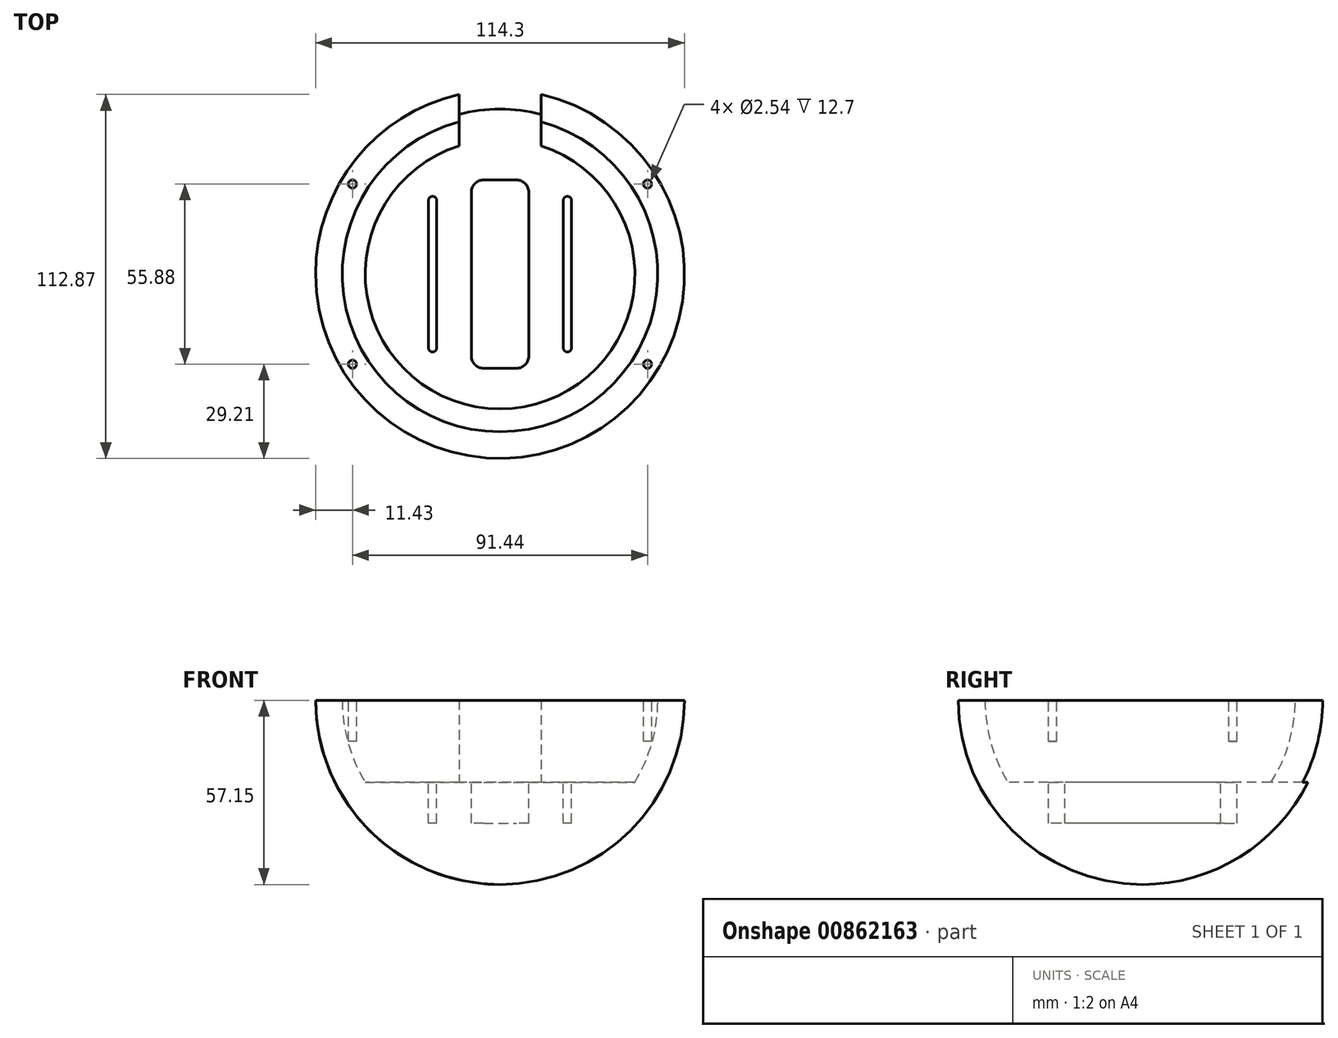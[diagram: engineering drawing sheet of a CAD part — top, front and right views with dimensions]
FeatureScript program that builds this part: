
annotation { "Feature Type Name" : "Feature", "Feature Type Description" : "" }
export const myFeature = defineFeature(function(context is Context, id is Id, definition is map)
    precondition{}
    {
        {
            var Q0;
            Q0=qCreatedBy(makeId("Front.planeOp"),FACE);
            var sketch = newSketch(context, id + "F0", { "sketchPlane" : qUnion([Q0])});
            skArc(sketch, "E0", {"start": v(-57.15, 0) * mm, "mid": v(-40.41, -40.41) * mm, "end": v(0, -57.15) * mm});
            skLineSegment(sketch, "E1", {"start": v(0, -25.4) * mm, "end": v(0, -57.15) * mm});
            skLineSegment(sketch, "E2", {"start": v(0, -57.15) * mm, "end": v(0, -25.4) * mm, "construction": true});
            skPoint(sketch, "E3.start.orphan", {"position": v(0, 31.75) * mm});
            skArc(sketch, "E4", {"start": v(-48.9, 0) * mm, "mid": v(-47.08, -13.19) * mm, "end": v(-41.78, -25.4) * mm});
            skLineSegment(sketch, "E5", {"start": v(0, -25.4) * mm, "end": v(-41.78, -25.4) * mm});
            skLineSegment(sketch, "E6", {"start": v(-57.15, 0) * mm, "end": v(-48.9, 0) * mm});
            skSolve(sketch);
        }
        {
            var Q0;
            Q0=makeQuery(id+"F0.imprint","IMPRINT",FACE,{"disambiguationData":[TD([[makeQuery(id+"F0.imprint","IMPRINT",EDGE,{"derivedFrom":sQuery(id+"F0.wireOp",EDGE,"E0")}),1.0]])]});
            var Q1;
            Q1=sQuery(id+"F0.wireOp",EDGE,"E1");
            revolve(context, id + "F1", {"surfaceOperationType" : NewSurfaceOperationType.NEW, "entities" : qUnion([Q0]), "axis" : qUnion([Q1]), "revolveType" : RevolveType.FULL});
        }
        {
            var Q0;
            Q0=makeQuery(id+"F1.opRevolve","SWEPT_FACE",FACE,{"disambiguationData":[OSD([sQuery(id+"F0.wireOp",EDGE,"E6")])]});
            var sketch = newSketch(context, id + "F2", { "sketchPlane" : qUnion([Q0])});
            skLineSegment(sketch, "E7", {"start": v(0, 0) * mm, "end": v(45.72, 0) * mm, "construction": true});
            skLineSegment(sketch, "E8", {"start": v(45.72, 0) * mm, "end": v(45.72, 27.94) * mm, "construction": true});
            skCircle(sketch, "E9", {"center": v(45.72, 27.94) * mm, "radius": 1.27 * mm});
            skCircle(sketch, "E10.MirrorC", {"center": v(45.72, -27.94) * mm, "radius": 1.27 * mm});
            skLineSegment(sketch, "E11.MirrorCS", {"start": v(45.72, 0) * mm, "end": v(45.72, -27.94) * mm, "construction": true});
            skLineSegment(sketch, "E12", {"start": v(0, 0) * mm, "end": v(0, -28.9) * mm, "construction": true});
            skCircle(sketch, "E13.MirrorC", {"center": v(-45.72, -27.94) * mm, "radius": 1.27 * mm});
            skCircle(sketch, "E14.MirrorC", {"center": v(-45.72, 27.94) * mm, "radius": 1.27 * mm});
            skSolve(sketch);
        }
        {
            var Q0;
            Q0 = qSketchRegion(id + "F2", true);
            extrude(context, id + "F3", {"entities" : qUnion([Q0]), "operationType" : NewBodyOperationType.REMOVE, "oppositeDirection" : true, "depth" : 12.7 * mm, "offsetDistance" : 25.4 * mm});
        }
        {
            var Q0;
            Q0=makeQuery(id+"F1.opRevolve","SWEPT_FACE",FACE,{"disambiguationData":[OSD([sQuery(id+"F0.wireOp",EDGE,"E5")])]});
            var sketch = newSketch(context, id + "F4", { "sketchPlane" : qUnion([Q0])});
            skLineSegment(sketch, "E15", {"start": v(0, 0) * mm, "end": v(41.78, 0) * mm, "construction": true});
            skLineSegment(sketch, "E16", {"start": v(0, 0) * mm, "end": v(-41.78, 0) * mm, "construction": true});
            skLineSegment(sketch, "E17", {"start": v(-20.89, 0) * mm, "end": v(-20.89, 22.86) * mm});
            skLineSegment(sketch, "E18", {"start": v(20.89, 0) * mm, "end": v(20.89, 22.86) * mm});
            skLineSegment(sketch, "E19.MirrorCS", {"start": v(-20.89, 0) * mm, "end": v(-20.89, -22.86) * mm});
            skLineSegment(sketch, "E20.MirrorCS", {"start": v(20.89, 0) * mm, "end": v(20.89, -22.86) * mm});
            skArc(sketch, "E21.0.startCap", {"start": v(-19.62, 0) * mm, "mid": v(-20.89, -1.27) * mm, "end": v(-22.16, 0) * mm});
            skArc(sketch, "E21.0.endCap", {"start": v(-22.16, 22.86) * mm, "mid": v(-20.89, 24.13) * mm, "end": v(-19.62, 22.86) * mm});
            skLineSegment(sketch, "E21.0.left", {"start": v(-22.16, 0) * mm, "end": v(-22.16, 22.86) * mm});
            skLineSegment(sketch, "E21.0.right", {"start": v(-19.62, 0) * mm, "end": v(-19.62, 22.86) * mm});
            skArc(sketch, "E21.1.startCap", {"start": v(-22.16, 0) * mm, "mid": v(-20.89, 1.27) * mm, "end": v(-19.62, 0) * mm});
            skArc(sketch, "E21.1.endCap", {"start": v(-19.62, -22.86) * mm, "mid": v(-20.89, -24.13) * mm, "end": v(-22.16, -22.86) * mm});
            skLineSegment(sketch, "E21.1.left", {"start": v(-19.62, 0) * mm, "end": v(-19.62, -22.86) * mm});
            skLineSegment(sketch, "E21.1.right", {"start": v(-22.16, 0) * mm, "end": v(-22.16, -22.86) * mm});
            skArc(sketch, "E22.0.startCap", {"start": v(22.16, 0) * mm, "mid": v(20.89, -1.27) * mm, "end": v(19.62, 0) * mm});
            skArc(sketch, "E22.0.endCap", {"start": v(19.62, 22.86) * mm, "mid": v(20.89, 24.13) * mm, "end": v(22.16, 22.86) * mm});
            skLineSegment(sketch, "E22.0.left", {"start": v(19.62, 0) * mm, "end": v(19.62, 22.86) * mm});
            skLineSegment(sketch, "E22.0.right", {"start": v(22.16, 0) * mm, "end": v(22.16, 22.86) * mm});
            skArc(sketch, "E22.1.startCap", {"start": v(19.62, 0) * mm, "mid": v(20.89, 1.27) * mm, "end": v(22.16, 0) * mm});
            skArc(sketch, "E22.1.endCap", {"start": v(22.16, -22.86) * mm, "mid": v(20.89, -24.13) * mm, "end": v(19.62, -22.86) * mm});
            skLineSegment(sketch, "E22.1.left", {"start": v(22.16, 0) * mm, "end": v(22.16, -22.86) * mm});
            skLineSegment(sketch, "E22.1.right", {"start": v(19.62, 0) * mm, "end": v(19.62, -22.86) * mm});
            skLineSegment(sketch, "E23.bottom", {"start": v(-5.08, 29.21) * mm, "end": v(5.08, 29.21) * mm});
            skLineSegment(sketch, "E23.top", {"start": v(-5.08, -29.21) * mm, "end": v(5.08, -29.21) * mm});
            skLineSegment(sketch, "E23.left", {"start": v(-8.89, 25.4) * mm, "end": v(-8.9, -25.4) * mm});
            skLineSegment(sketch, "E23.right", {"start": v(8.9, 25.4) * mm, "end": v(8.89, -25.4) * mm});
            skPoint(sketch, "E23.middle", {"position": v(0, 0) * mm});
            skPoint(sketch, "E24.visualSharp", {"position": v(-8.89, 29.21) * mm});
            skArc(sketch, "E24.filletArc", {"start": v(-5.08, 29.21) * mm, "mid": v(-7.77, 28.1) * mm, "end": v(-8.89, 25.4) * mm});
            skPoint(sketch, "E25.visualSharp", {"position": v(8.9, 29.21) * mm});
            skArc(sketch, "E25.filletArc", {"start": v(8.9, 25.4) * mm, "mid": v(7.77, 28.1) * mm, "end": v(5.08, 29.21) * mm});
            skPoint(sketch, "E26.visualSharp", {"position": v(8.89, -29.21) * mm});
            skArc(sketch, "E26.filletArc", {"start": v(5.08, -29.21) * mm, "mid": v(7.77, -28.1) * mm, "end": v(8.89, -25.4) * mm});
            skPoint(sketch, "E27.visualSharp", {"position": v(-8.9, -29.21) * mm});
            skArc(sketch, "E27.filletArc", {"start": v(-8.9, -25.4) * mm, "mid": v(-7.77, -28.1) * mm, "end": v(-5.08, -29.21) * mm});
            skLineSegment(sketch, "E28", {"start": v(-34.97, 22.86) * mm, "end": v(34.97, 22.86) * mm, "construction": true});
            skSolve(sketch);
        }
        {
            var Q0;
            Q0 = qSketchRegion(id + "F4", true);
            extrude(context, id + "F5", {"entities" : qUnion([Q0]), "operationType" : NewBodyOperationType.REMOVE, "oppositeDirection" : true, "depth" : 12.7 * mm, "offsetDistance" : 25.4 * mm});
        }
        {
            var Q0;
            Q0=makeQuery(id+"F1.opRevolve","SWEPT_FACE",FACE,{"disambiguationData":[OSD([sQuery(id+"F0.wireOp",EDGE,"E6")])]});
            var sketch = newSketch(context, id + "F6", { "sketchPlane" : qUnion([Q0])});
            skLineSegment(sketch, "E29.bottom", {"start": v(12.7, 72.64) * mm, "end": v(-12.7, 72.64) * mm});
            skLineSegment(sketch, "E29.left", {"start": v(12.7, 72.64) * mm, "end": v(12.7, 30.24) * mm});
            skLineSegment(sketch, "E29.right", {"start": v(-12.7, 72.64) * mm, "end": v(-12.7, 30.24) * mm});
            skPoint(sketch, "E29.middle", {"position": v(0, 48.9) * mm});
            skLineSegment(sketch, "E30", {"start": v(-12.7, 30.24) * mm, "end": v(12.7, 30.24) * mm});
            skSolve(sketch);
        }
        {
            var Q0;
            Q0 = qSketchRegion(id + "F6", true);
            extrude(context, id + "F7", {"entities" : qUnion([Q0]), "operationType" : NewBodyOperationType.REMOVE, "oppositeDirection" : true, "depth" : 25.4 * mm, "offsetDistance" : 25.4 * mm});
        }
    });
